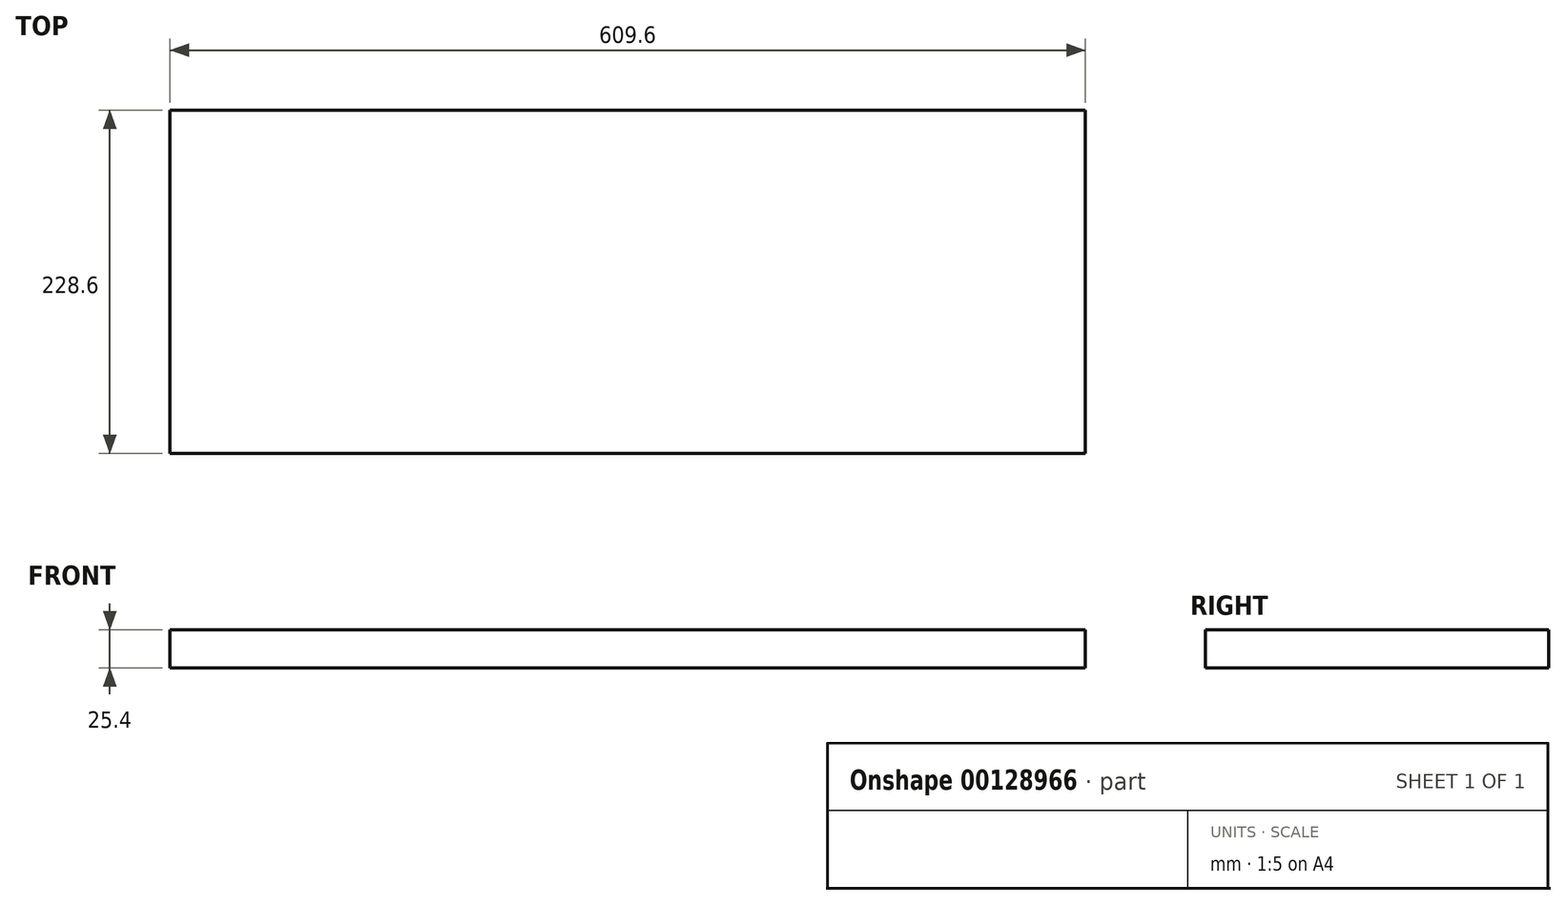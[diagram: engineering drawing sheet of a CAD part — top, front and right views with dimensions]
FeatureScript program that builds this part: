
annotation { "Feature Type Name" : "Feature", "Feature Type Description" : "" }
export const myFeature = defineFeature(function(context is Context, id is Id, definition is map)
    precondition{}
    {
        {
            var Q0;
            Q0=qCreatedBy(makeId("Top.planeOp"),FACE);
            var sketch = newSketch(context, id + "F0", { "sketchPlane" : qUnion([Q0])});
            skLineSegment(sketch, "E0.bottom", {"start": v(0, 0) * mm, "end": v(-609.6, 0) * mm});
            skLineSegment(sketch, "E0.top", {"start": v(0, 228.6) * mm, "end": v(-609.6, 228.6) * mm});
            skLineSegment(sketch, "E0.left", {"start": v(0, 0) * mm, "end": v(0, 228.6) * mm});
            skLineSegment(sketch, "E0.right", {"start": v(-609.6, 0) * mm, "end": v(-609.6, 228.6) * mm});
            skSolve(sketch);
        }
        {
            var Q0;
            Q0 = qSketchRegion(id + "F0", true);
            extrude(context, id + "F1", {"entities" : qUnion([Q0]), "depth" : 25.4 * mm});
        }
    });
